# Revit family: COALESSE_AWAIT_-_Round_Table_8680
name_source: partatom
category: Мебель
revit_build: Autodesk Revit 2017 (Build: 20160225_1515(x64)
units: mm (PartAtom-declared; Revit-internal decimal feet)

## family parameters
Всегда вертикально = Да
На основе рабочей плоскости = Нет
Общий = Нет
При загрузке вырезать с полостями = Нет
Точка расчета площади = Нет

## types (4) — shared parameters
Base = Furniture_Coalesse_Await - Table Base
Diameter = 1' - 3 3/4"
Edging = Furniture_Coalesse_Await - Table Edging
Glass Top = Furniture_Coalesse_Await - Table Top (Glass)
Laminate Top = Furniture_Coalesse_Await - Table Top (Laminate)
R = 0' - 7 7/8"
URL = www.coalesse.com
Группа модели = Await
Изготовитель = COALESSE

## per-type parameters (varying)
| type | GLASS | Height | LAMINATE | Комментарии к типоразмеру | Описание | Стоимость |
| 19"H, Laminate Top | Нет | 1' - 7" | Да | 46-T1 | Await, Freestanding Low Table, Laminate Top | 895 $ |
| 25"H, Laminate Top | Нет | 2' - 1" | Да | 46-T2 | Await, Freestanding Low Table, Laminate Top | 1169 $ |
| 25"H, Glass Top | Да | 2' - 1" | Нет | 46-T2 | Await, Freestanding Low Table, Glass Top | 1450 $ |
| 19"H, Glass Top | Да | 1' - 7" | Нет | 46-T1 | Await, Freestanding Low Table, Glass Top | 1176 $ |

## geometry (parser evidence)
native form markers: Sweep x1
no freeform markers — native parametric forms only
